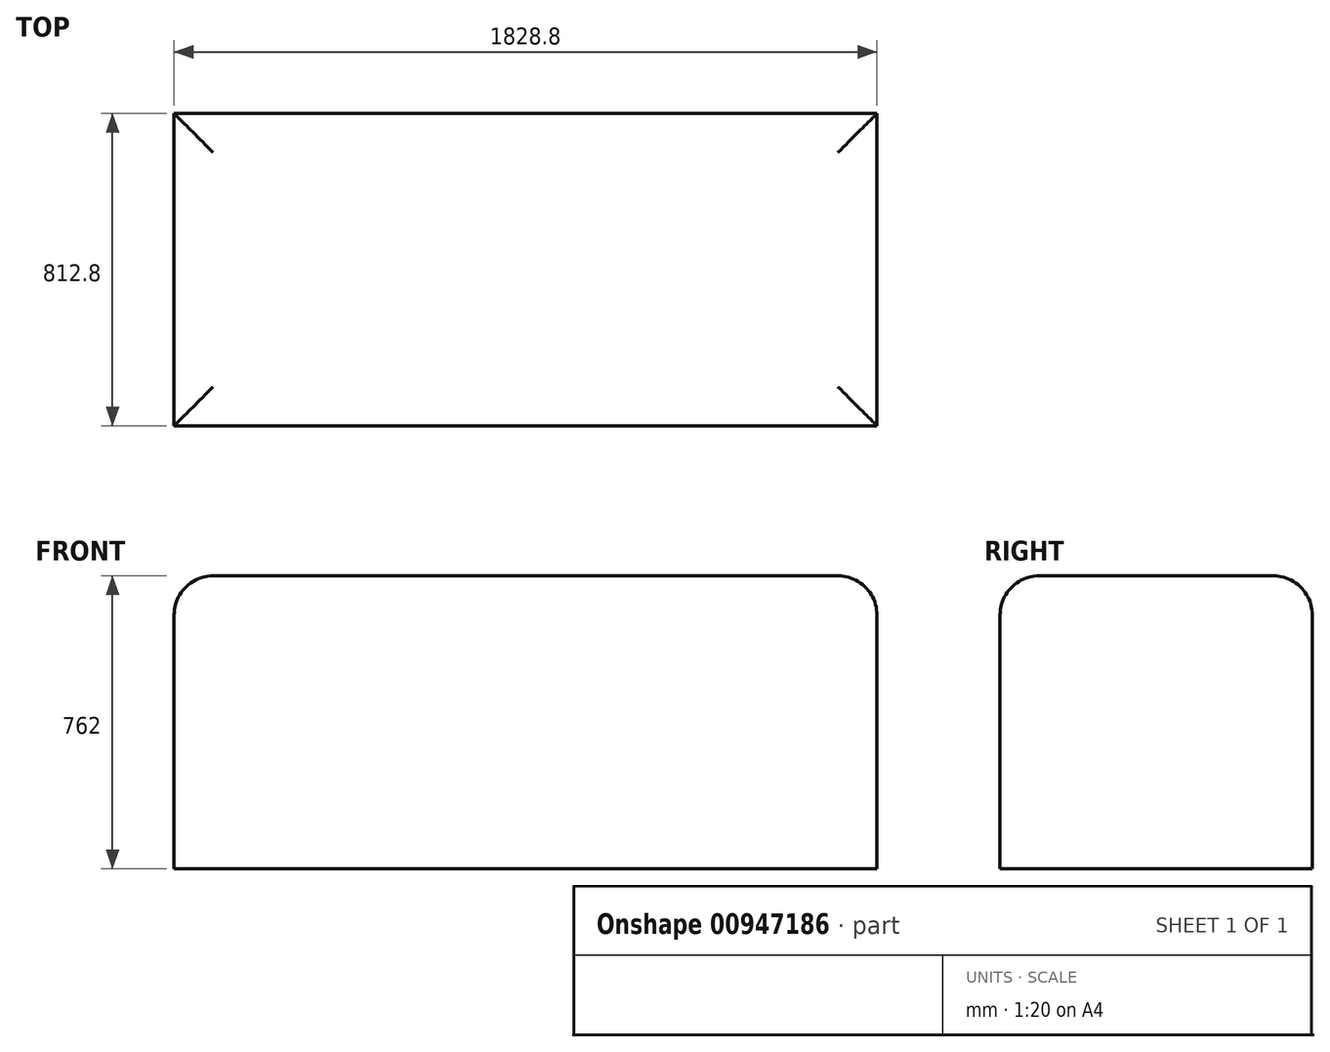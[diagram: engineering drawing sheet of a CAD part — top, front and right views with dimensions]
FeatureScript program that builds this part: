
annotation { "Feature Type Name" : "Feature", "Feature Type Description" : "" }
export const myFeature = defineFeature(function(context is Context, id is Id, definition is map)
    precondition{}
    {
        {
            var Q0;
            Q0=qCreatedBy(makeId("Top.planeOp"),FACE);
            var sketch = newSketch(context, id + "F0", { "sketchPlane" : qUnion([Q0])});
            skLineSegment(sketch, "E0.bottom", {"start": v(0, 0) * mm, "end": v(1828.8, 0) * mm});
            skLineSegment(sketch, "E0.top", {"start": v(0, 812.8) * mm, "end": v(1828.8, 812.8) * mm});
            skLineSegment(sketch, "E0.left", {"start": v(0, 0) * mm, "end": v(0, 812.8) * mm});
            skLineSegment(sketch, "E0.right", {"start": v(1828.8, 0) * mm, "end": v(1828.8, 812.8) * mm});
            skSolve(sketch);
        }
        {
            var Q0;
            Q0 = qSketchRegion(id + "F0", true);
            extrude(context, id + "F1", {"entities" : qUnion([Q0]), "depth" : 762 * mm, "offsetDistance" : 25.4 * mm});
        }
        {
            var Q0;
            Q0=makeQuery(id+"F1.opExtrude","CAP_EDGE",EDGE,{"disambiguationData":[OSD([sQuery(id+"F0.wireOp",EDGE,"E0.left")])],"isStart":false});
            var Q1;
            Q1=makeQuery(id+"F1.opExtrude","CAP_EDGE",EDGE,{"disambiguationData":[OSD([sQuery(id+"F0.wireOp",EDGE,"E0.top")])],"isStart":false});
            var Q2;
            Q2=makeQuery(id+"F1.opExtrude","CAP_EDGE",EDGE,{"disambiguationData":[OSD([sQuery(id+"F0.wireOp",EDGE,"E0.right")])],"isStart":false});
            var Q3;
            Q3=makeQuery(id+"F1.opExtrude","CAP_EDGE",EDGE,{"disambiguationData":[OSD([sQuery(id+"F0.wireOp",EDGE,"E0.bottom")])],"isStart":false});
            fillet(context, id + "F2", {"entities" : qUnion([Q0, Q1, Q2, Q3]), "radius" : 101.6 * mm, "tangentPropagation" : true, "allowEdgeOverflow" : false});
        }
    });
